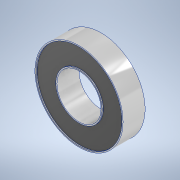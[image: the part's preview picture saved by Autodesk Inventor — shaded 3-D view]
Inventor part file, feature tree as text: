
AUTODESK INVENTOR PART (.ipt)
format: ipt  version: 2020.1 (Build 241239000, 239)  size: 151,040 bytes
history: native  units: mm
features: extrude x3, sketch x3
ambient origin geometry x8: Origin, YZ Plane, XZ Plane, XY Plane, X Axis, Y Axis, Z Axis, Center Point
bodies: Solid1 (feature_tree)
feature tree (6):
  extrude  "Extrusion1"  Depth=10.0mm
  extrude  "Extrusion2"  Depth=4.5mm
  extrude  "Extrusion3"  Depth=0.25mm
  sketch  "Sketch1"  dims[d0=10.0mm d1=20.0mm]
  sketch  "Sketch2"  dims[d2=4.5mm d3=0.0mm d4=19.5mm]
  sketch  "Sketch3"  dims[d5=10.0mm d6=10.5mm d7=0.25mm d8=0.0mm d9=20.0mm d10=19.5mm d11=10.0mm d12=10.5mm d13=0.25mm d14=0.0mm]
